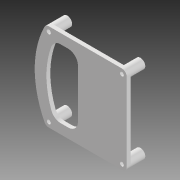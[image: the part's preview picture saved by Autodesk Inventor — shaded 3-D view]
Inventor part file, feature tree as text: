
AUTODESK INVENTOR PART (.ipt)
format: ipt  version: 2021 (Build 250183000, 183)  size: 148,480 bytes
history: native  units: in
note: dims shown in document units (in); Inventor stores cm internally (conversion verified against a paired STEP export)
features: extrude x2, sketch x2, reference x2, other x2, fillet x1
ambient origin geometry x8: Origin, YZ Plane, XZ Plane, XY Plane, X Axis, Y Axis, Z Axis, Center Point
bodies: Solid1 (feature_tree)
feature tree (9):
  extrude  "Extrusion1"  Depth=0.3937in
  extrude  "Extrusion2"  Depth=0.3937in
  fillet  "Fillet1"  Radius=0.4724in
  sketch  "Sketch1"  dims[d0=0.5906in d1=0.0in d2=0.3937in]
  reference  "Reference1"
  sketch  "Sketch2"  dims[d3=0.3937in d4=1.9685in d5=0.4724in d6=0.1575in d7=0.0in d8=0.3937in]
  reference  "Reference2"
  other  "Impedance_Analyzer_V2.iam"
  other  "Bottom Case:1"
